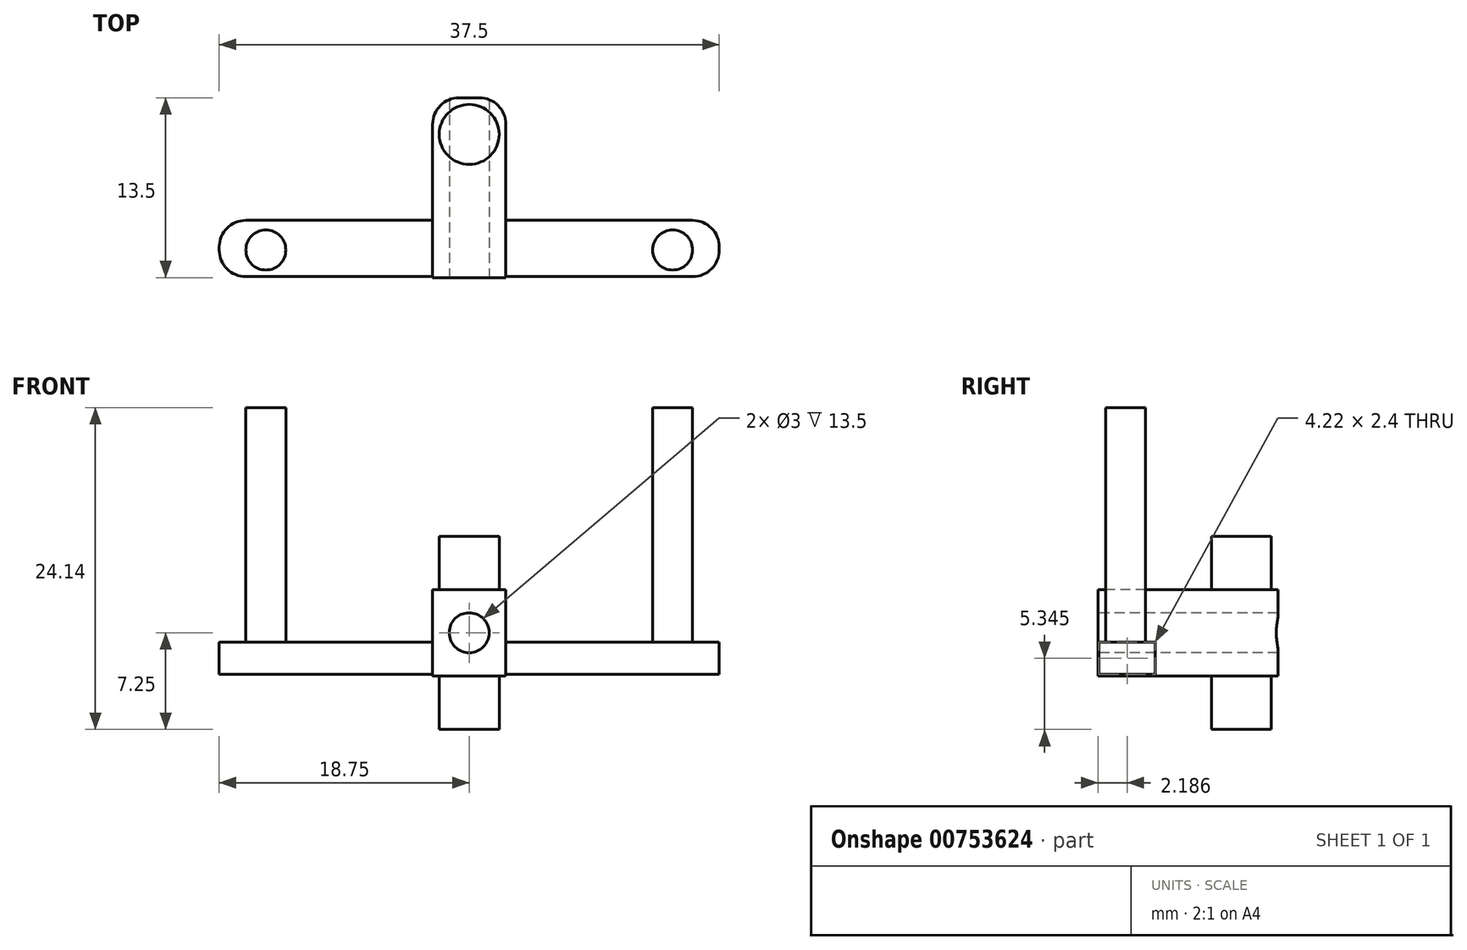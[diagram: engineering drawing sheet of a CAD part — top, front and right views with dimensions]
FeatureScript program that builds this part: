
annotation { "Feature Type Name" : "Feature", "Feature Type Description" : "" }
export const myFeature = defineFeature(function(context is Context, id is Id, definition is map)
    precondition{}
    {
        {
            var Q0;
            Q0=qCreatedBy(makeId("Top.planeOp"),FACE);
            var sketch = newSketch(context, id + "F0", { "sketchPlane" : qUnion([Q0])});
            skCircle(sketch, "E0", {"center": v(0, 0) * mm, "radius": 2.25 * mm});
            skSolve(sketch);
        }
        {
            var Q0;
            Q0=makeQuery(id+"F0.imprint","IMPRINT",FACE,{"disambiguationData":[TD([[makeQuery(id+"F0.imprint","IMPRINT",EDGE,{"derivedFrom":sQuery(id+"F0.wireOp",EDGE,"E0")}),1.0]])]});
            var Q1;
            Q1 = qSketchRegion(id + "F0", true);
            extrude(context, id + "F1", {"entities" : qUnion([Q0, Q1]), "depth" : 4 * mm, "offsetDistance" : 25 * mm});
        }
        {
            var Q0;
            Q0=makeQuery(id+"F1.opExtrude","CAP_FACE",FACE,{"disambiguationData":[OSD([sQuery(id+"F0.wireOp",EDGE,"E0")])],"isStart":false});
            var sketch = newSketch(context, id + "F2", { "sketchPlane" : qUnion([Q0])});
            skLineSegment(sketch, "E1.bottom", {"start": v(-2.75, 2.75) * mm, "end": v(2.75, 2.75) * mm});
            skLineSegment(sketch, "E1.top", {"start": v(-2.75, -2.75) * mm, "end": v(2.75, -2.75) * mm});
            skLineSegment(sketch, "E1.left", {"start": v(-2.75, 2.75) * mm, "end": v(-2.75, -2.75) * mm});
            skLineSegment(sketch, "E1.right", {"start": v(2.75, 2.75) * mm, "end": v(2.75, -2.75) * mm});
            skPoint(sketch, "E1.middle", {"position": v(0, 0) * mm});
            skSolve(sketch);
        }
        {
            var Q0;
            Q0 = qSketchRegion(id + "F2", true);
            extrude(context, id + "F3", {"entities" : qUnion([Q0]), "operationType" : NewBodyOperationType.ADD, "depth" : 6.5 * mm, "offsetDistance" : 25 * mm});
        }
        {
            var Q0;
            Q0=makeQuery(id+"F3.opExtrude","CAP_FACE",FACE,{"disambiguationData":[OSD([sQuery(id+"F2.wireOp",EDGE,"E1.bottom"),sQuery(id+"F2.wireOp",EDGE,"E1.top"),sQuery(id+"F2.wireOp",EDGE,"E1.left"),sQuery(id+"F2.wireOp",EDGE,"E1.right")])],"isStart":false});
            var sketch = newSketch(context, id + "F4", { "sketchPlane" : qUnion([Q0])});
            skCircle(sketch, "E2", {"center": v(0, 0) * mm, "radius": 2.25 * mm});
            skSolve(sketch);
        }
        {
            var Q0;
            Q0 = qSketchRegion(id + "F4", true);
            extrude(context, id + "F5", {"entities" : qUnion([Q0]), "operationType" : NewBodyOperationType.ADD, "depth" : 4 * mm, "offsetDistance" : 25 * mm});
        }
        {
            var Q0;
            Q0=makeQuery(id+"F3.opExtrude","SWEPT_FACE",FACE,{"disambiguationData":[OSD([sQuery(id+"F2.wireOp",EDGE,"E1.top")])]});
            extrude(context, id + "F6", {"entities" : qUnion([Q0]), "operationType" : NewBodyOperationType.ADD, "depth" : 8 * mm, "offsetDistance" : 25 * mm});
        }
        {
            var Q0;
            Q0=makeQuery(id+"F6.opExtrude","CAP_FACE",FACE,{"disambiguationData":[OSD([sQuery(id+"F2.wireOp",EDGE,"E1.top")])],"isStart":false});
            var sketch = newSketch(context, id + "F7", { "sketchPlane" : qUnion([Q0])});
            skCircle(sketch, "E3", {"center": v(0, 7.25) * mm, "radius": 1.5 * mm});
            skSolve(sketch);
        }
        {
            var Q0;
            Q0 = qSketchRegion(id + "F7", true);
            extrude(context, id + "F8", {"entities" : qUnion([Q0]), "operationType" : NewBodyOperationType.REMOVE, "endBound" : BoundingType.UP_TO_NEXT, "oppositeDirection" : true, "depth" : 25 * mm, "offsetDistance" : 25 * mm});
        }
        {
            var Q0;
            Q0=makeQuery(id+"F3.opExtrude","SWEPT_EDGE",EDGE,{"disambiguationData":[OSD([sQuery(id+"F2.wireOp",EDGE,"E1.bottom"),sQuery(id+"F2.wireOp",EDGE,"E1.left")])]});
            var Q1;
            Q1=makeQuery(id+"F3.opExtrude","SWEPT_EDGE",EDGE,{"disambiguationData":[OSD([sQuery(id+"F2.wireOp",EDGE,"E1.bottom"),sQuery(id+"F2.wireOp",EDGE,"E1.right")])]});
            fillet(context, id + "F9", {"entities" : qUnion([Q0, Q1]), "radius" : 2 * mm, "tangentPropagation" : true, "allowEdgeOverflow" : false});
        }
        {
            var Q0;
            {var subQ0=sQuery(id+"F2.wireOp",EDGE,"E1.right");Q0=makeQuery(id+"F6.boolean.opBoolean","MERGE",FACE,{"derivedFrom":[makeQuery(id+"F3.opExtrude","SWEPT_FACE",FACE,{"disambiguationData":[OSD([subQ0])]}),makeQuery(id+"F6.opExtrude","SWEPT_FACE",FACE,{"disambiguationData":[OSD([sQuery(id+"F2.wireOp",EDGE,"E1.top"),subQ0])]})]});}
            var sketch = newSketch(context, id + "F10", { "sketchPlane" : qUnion([Q0])});
            skSolve(sketch);
        }
        {
            var Q0;
            {var subQ0=sQuery(id+"F2.wireOp",EDGE,"E1.right");var subQ1=sQuery(id+"F2.wireOp",EDGE,"E1.top");Q0=makeQuery(id+"F10.imprint","IMPRINT",FACE,{"disambiguationData":[TD([[makeQuery(id+"F10.imprint","IMPRINT",EDGE,{"derivedFrom":makeQuery(id+"F6.opExtrude","CAP_EDGE",EDGE,{"disambiguationData":[OSD([subQ1,subQ0])],"isStart":false})}),1.0]])]});}
            var sketch = newSketch(context, id + "F11", { "sketchPlane" : qUnion([Q0])});
            skLineSegment(sketch, "E4.bottom", {"start": v(-10.68, 4.14) * mm, "end": v(-6.45, 4.14) * mm});
            skLineSegment(sketch, "E4.top", {"start": v(-10.68, 6.55) * mm, "end": v(-6.45, 6.55) * mm});
            skLineSegment(sketch, "E4.left", {"start": v(-10.68, 4.14) * mm, "end": v(-10.68, 6.55) * mm});
            skLineSegment(sketch, "E4.right", {"start": v(-6.45, 4.14) * mm, "end": v(-6.45, 6.55) * mm});
            skSolve(sketch);
        }
        {
            var Q0;
            Q0 = qSketchRegion(id + "F11", true);
            extrude(context, id + "F12", {"entities" : qUnion([Q0]), "operationType" : NewBodyOperationType.ADD, "depth" : 16 * mm, "offsetDistance" : 25 * mm});
        }
        {
            var Q0;
            Q0=makeQuery(id+"F12.opExtrude","CAP_EDGE",EDGE,{"disambiguationData":[OSD([sQuery(id+"F11.wireOp",EDGE,"E4.left")])],"isStart":false});
            var Q1;
            Q1=makeQuery(id+"F12.opExtrude","CAP_EDGE",EDGE,{"disambiguationData":[OSD([sQuery(id+"F11.wireOp",EDGE,"E4.right")])],"isStart":false});
            fillet(context, id + "F13", {"entities" : qUnion([Q0, Q1]), "radius" : 2 * mm, "tangentPropagation" : true, "allowEdgeOverflow" : false});
        }
        {
            var Q0;
            Q0=makeQuery(id+"F12.opExtrude","SWEPT_FACE",FACE,{"disambiguationData":[OSD([sQuery(id+"F11.wireOp",EDGE,"E4.bottom")])]});
            var sketch = newSketch(context, id + "F14", { "sketchPlane" : qUnion([Q0])});
            skCircle(sketch, "E5", {"center": v(15.25, 8.68) * mm, "radius": 1.5 * mm});
            skSolve(sketch);
        }
        {
            var Q0;
            Q0=makeQuery(id+"F14.imprint","IMPRINT",FACE,{"disambiguationData":[TD([[makeQuery(id+"F14.imprint","IMPRINT",EDGE,{"derivedFrom":sQuery(id+"F14.wireOp",EDGE,"E5")}),1.0]])]});
            extrude(context, id + "F15", {"entities" : qUnion([Q0]), "operationType" : NewBodyOperationType.ADD, "depth" : -20 * mm, "offsetDistance" : 25 * mm});
        }
        {
            var Q0;
            Q0=makeQuery(id+"F1.opExtrude","SWEPT_BODY",BODY,{"disambiguationData":[OSD([sQuery(id+"F0.wireOp",EDGE,"E0")])]});
            var Q1;
            Q1=qCreatedBy(makeId("Right.planeOp"),FACE);
            mirror(context, id + "F16", {"entities" : qUnion([Q0]), "mirrorPlane" : qUnion([Q1])});
        }
    });
